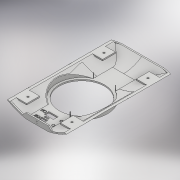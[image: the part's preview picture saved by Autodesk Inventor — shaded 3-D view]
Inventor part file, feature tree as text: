
AUTODESK INVENTOR PART (.ipt)
format: ipt  version: 2017 (Build 210142000, 142)  size: 1,726,976 bytes
history: native  units: mm
features: sketch x30, extrude x28, projected_geometry x19, plane x3, fillet x1, loft x1, mirror x1, shell x1, other x1
ambient origin geometry x8: Origin, YZ Plane, XZ Plane, XY Plane, X Axis, Y Axis, Z Axis, Center Point
bodies: Solid1 (feature_tree)
feature tree (85):
  extrude  "Extrusion1"  Depth=35.0mm
  extrude  "Extrusion2"  Depth=9.0mm TaperAngle=0.0deg
  extrude  "Extrusion6"  Depth=70.0mm TaperAngle=0.0deg
  extrude  "Extrusion9"  Depth=10.0mm
  extrude  "Extrusion11"  Depth=200.0mm
  fillet  "Fillet2"  [1 undecoded]
  sketch  "Sketch29"  dims[d72=0.0mm d73=90.0deg d81=2.0mm d83=-324.476mm]
  plane  "Work Plane8"
  loft  "Loft1"
  mirror  "Mirror8"
  shell  "Shell3"  Thickness=-324.476mm
  plane  "Work Plane9"
  extrude  "Extrusion16"  [1 undecoded]
  plane  "Work Plane10"
  extrude  "Extrusion17"  Depth=1.5mm TaperAngle=0.0deg
  extrude  "Extrusion18"  Depth=3.0mm TaperAngle=0.0deg
  extrude  "Extrusion19"  Depth=173.6141mm TaperAngle=0.0deg
  extrude  "Extrusion20"  Depth=200.0mm TaperAngle=0.0deg
  extrude  "Extrusion21"  Depth=20.0mm
  extrude  "Extrusion22"  Depth=20.0mm
  extrude  "Extrusion24"  Depth=20.0mm
  extrude  "Extrusion25"  Depth=20.0mm
  extrude  "Extrusion26"  Depth=20.0mm TaperAngle=0.0deg
  extrude  "Extrusion27"  Depth=3.0mm
  extrude  "Extrusion28"  Depth=3.0mm
  extrude  "Extrusion30"  Depth=20.0mm TaperAngle=0.0deg
  extrude  "Extrusion31"  Depth=7.0mm
  extrude  "Extrusion32"  Depth=7.0mm
  extrude  "Extrusion33"  Depth=7.2mm
  extrude  "Extrusion34"  Depth=10.0mm TaperAngle=0.0deg
  extrude  "Extrusion35"  Depth=8.0mm
  extrude  "Extrusion36"  Depth=8.0mm
  extrude  "Extrusion37"  Depth=1.9mm TaperAngle=0.0deg
  extrude  "Extrusion39"  Depth=79.0mm
  extrude  "Extrusion41"  Depth=77.0mm
  extrude  "Extrusion42"  Depth=2.0mm TaperAngle=0.0deg
  sketch  "Sketch1"  dims[d0=63.0mm d1=0.0mm d2=35.0mm]
  sketch  "Sketch3"  dims[d3=150.0mm d4=9.0mm d5=0.0mm]
  sketch  "Sketch12"  dims[d30=250.0mm d31=0.0mm d48=70.0mm d49=0.0mm]
  sketch  "Sketch17"  dims[d53=70.0mm d54=0.0mm d55=10.0mm]
  sketch  "Sketch20"  dims[d68=-347.0mm d69=200.0mm d70=0.0mm d71=90.0deg]
  projected_geometry  "Projected Loop9"
  sketch  "Sketch30"  dims[d93=2.5mm d94=0.0mm d96=-15.524mm]
  other  "Edges1"
  sketch  "Sketch37"  dims[d102=4.0mm d103=0.0mm d104=1.5mm d105=0.0mm]
  sketch  "Sketch38"  dims[d106=2.0mm d107=0.0mm d111=3.0mm d112=0.0mm]
  sketch  "Sketch39"  dims[d113=12.0mm d114=0.0mm d115=173.6141mm d116=0.0mm]
  projected_geometry  "Projected Loop13"
  projected_geometry  "Projected Loop14"
  sketch  "Sketch41"  dims[d119=2.0mm d120=0.0mm d121=200.0mm d122=0.0mm]
  sketch  "Sketch43"  dims[d123=20.0mm d124=20.0mm]
  sketch  "Sketch44"  dims[d125=20.0mm d126=20.0mm]
  projected_geometry  "Projected Loop15"
  projected_geometry  "Projected Loop16"
  sketch  "Sketch46"  dims[d127=20.0mm d128=20.0mm]
  sketch  "Sketch50"  dims[d129=20.0mm d130=20.0mm]
  sketch  "Sketch51"  dims[d131=2.0mm d132=0.0mm d133=20.0mm d134=0.0mm]
  sketch  "Sketch52"  dims[d135=20.0mm d136=0.0mm d147=3.0mm]
  sketch  "Sketch53"  dims[d148=3.0mm d149=3.0mm]
  projected_geometry  "Projected Loop17"
  projected_geometry  "Projected Loop18"
  sketch  "Sketch54"  dims[d150=3.0mm d151=20.0mm d152=0.0mm]
  projected_geometry  "Projected Loop19"
  projected_geometry  "Projected Loop20"
  sketch  "Sketch56"  dims[d153=7.0mm d154=7.0mm]
  projected_geometry  "Projected Loop21"
  sketch  "Sketch57"  dims[d155=7.0mm d156=7.0mm]
  sketch  "Sketch59"  dims[d157=20.0mm d158=0.0mm d163=7.2mm]
  sketch  "Sketch60"  dims[d167=4.0mm d170=10.0mm d171=0.0mm]
  projected_geometry  "Projected Loop23"
  projected_geometry  "Projected Loop24"
  projected_geometry  "Projected Loop25"
  projected_geometry  "Projected Loop26"
  projected_geometry  "Projected Loop27"
  sketch  "Sketch61"  dims[d172=1.0mm d173=0.0mm d174=8.0mm]
  sketch  "Sketch62"  dims[d175=8.0mm d176=8.0mm]
  projected_geometry  "Projected Loop28"
  projected_geometry  "Projected Loop29"
  projected_geometry  "Projected Loop30"
  projected_geometry  "Projected Loop31"
  sketch  "Sketch63"  dims[d177=8.0mm d178=1.9mm d179=0.0mm]
  sketch  "Sketch64"  dims[d180=1.9mm d181=0.0mm d183=79.0mm]
  sketch  "Sketch66"  dims[d184=50.0mm d185=0.0mm d186=77.0mm]
  sketch  "Sketch70"  dims[d187=79.0mm d188=2.0mm d189=0.0mm]
  sketch  "Sketch71"  dims[d192=7.8mm d193=0.0mm d197=90.0deg d198=80.0mm d199=0.0mm d200=70.0mm d201=2.0mm d202=0.0mm]
note: 2 required parameter values undecoded (feature->parameter linkage not recoverable at this tier; creation-order binding heuristic only, values carry confidence <= 0.55)
